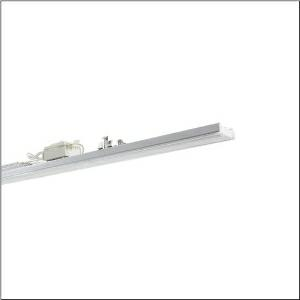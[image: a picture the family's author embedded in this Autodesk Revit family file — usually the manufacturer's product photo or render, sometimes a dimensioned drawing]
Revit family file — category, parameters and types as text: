
# Revit family: licross_11_recessed_mo_51te10dv4e5g
name_source: partatom
category: Lighting Fixtures
units: mm (PartAtom-declared; Revit-internal decimal feet)

## family parameters
Cut with Voids When Loaded = No
Host = Face
Light Source = No
Part Type = Normal
Room Calculation Point = No
Round Connector Dimension = Use Diameter
Shared = No

## types (1)
- --- (1 x LED, 14930 lm, 84.1 W, 4000K)
    Apparent Load = 84 VA
    CIE Flux Codes = 50 81 96 100 100
    Color Rendering = 80
    Color Temperature = 4000K
    Default Elevation = 1800 mm
    Description = Licross 11 Recessed MO, luminaire insert, of sheet steel, galvanised, coil coated, white, length: 2.250mm, width: 66mm, height: 67mm, LED rated luminous flux: 14.930lm, light colour: 840, SDCM (Standard Deviation of Colour Matching)MacAdam ≤ 2 SDCM (initial), control gear: DALI 2, with plug, 5-pole, with phase selection, mains connection: 220..240V, AC, 50/60Hz, rated input power: 84W, internal wiring halogen-free, primary optical cover: cover, of PMMA, light emission: direct distribution, primary light characteristic: symmetric, protection rating (complete): IP54, insulation class (complete): insulation class I (protective earthing), certification: CE, ENEC, VDE, UKCA, protection symbol: D if used in an environment with non-conductive dust loads with corresponding accessories, impact resistance: IK06, permissible ambient temperature for indoor applications: -25..+35°C, corresponds to IFS (International Featured Standards) requirements for safety and quality in the food industry, reducing of maximum allowable ambient temperature of 5°C with ceiling mounting, LABS conformity tested according to VDMA 24364:2018-05, The light source and the operating device comply with the requirements of the Ecodesign Regulation (EU) 2019/2020 and are replaceable in accordance with this regulation, packaging unit: 1 piece
    Height = 58 mm
    Lamp = 1 x LED
    Lamp Light Flux = 14930 lm
    Lamp Power = 84.1 W
    Lamp count = 1
    Length = 2250 mm
    Luminous efficacy = 178 lm/W
    Manufacturer = Siteco
    ModVariant = No
    Model = 51TE10DV4E5G
    Mounting Place = Ceiling
    Mounting Type = Pendant
    Number of Poles = 1
    OnlyDefault = Yes
    Power Factor = 1
    Product Name = Licross 11 Recessed MO
    Product group = luminaire insert | ceiling pendant
    ProductGroupID = 901
    Protection Class = Protection class I
    Protection Degree = IP 54
    RLX_Detail_Level = 1
    RLX_Emergency_Light_Flux = 0 lm
    RLX_Emergency_Type = 0
    RLX_Emergency_Type_DB = No
    RlxData = <blob elided: 29689 chars, md5=270e673c>
    Socket = socket
    Standby Power = 0 W
    System Light Flux = 14930 lm
    System Power = 84 W
    Type Comments = factory setting: luminous flux: 100 % | dim-lin: 254 | 378 mA
    Type Image = l_1296930.jpg
    URL = http://relux.com
    VarID = @adj_101313
    Voltage = 0 V
    Weight = 0.00 kg
    Width = 66 mm

## geometry (parser evidence)
native form markers: Blend x4, Sweep x11
no freeform markers — native parametric forms only
